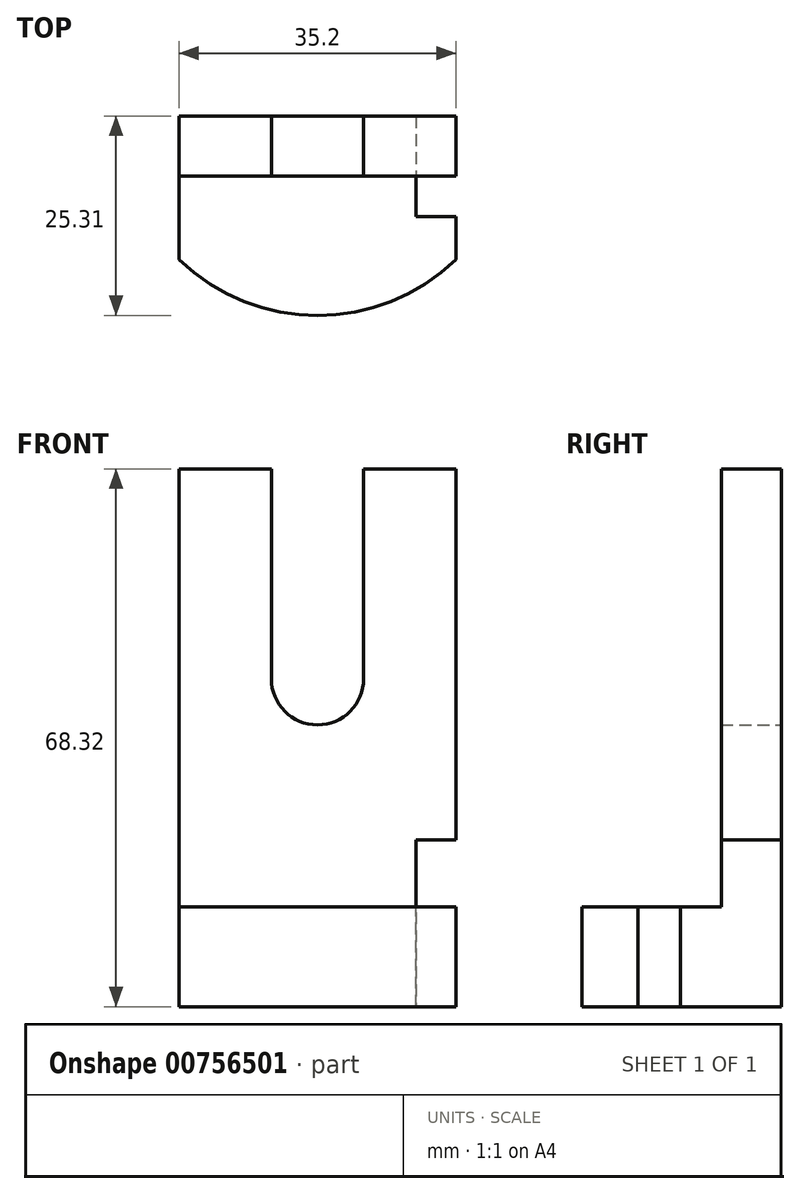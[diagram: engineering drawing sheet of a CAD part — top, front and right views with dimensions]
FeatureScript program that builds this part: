
annotation { "Feature Type Name" : "Feature", "Feature Type Description" : "" }
export const myFeature = defineFeature(function(context is Context, id is Id, definition is map)
    precondition{}
    {
        {
            var Q0;
            Q0=qCreatedBy(makeId("Top.planeOp"),FACE);
            var sketch = newSketch(context, id + "F0", { "sketchPlane" : qUnion([Q0])});
            skLineSegment(sketch, "E0", {"start": v(17.6, 0) * mm, "end": v(-17.6, 0) * mm});
            skLineSegment(sketch, "E1", {"start": v(-17.6, 0) * mm, "end": v(-17.6, -18.2) * mm});
            skArc(sketch, "E2", {"start": v(-17.6, -18.2) * mm, "mid": v(0, -25.31) * mm, "end": v(17.6, -18.2) * mm});
            skLineSegment(sketch, "E3", {"start": v(17.6, 0) * mm, "end": v(17.6, -18.2) * mm});
            skSolve(sketch);
        }
        {
            var Q0;
            Q0 = qSketchRegion(id + "F0", true);
            extrude(context, id + "F1", {"entities" : qUnion([Q0]), "depth" : 12.7 * mm, "offsetDistance" : 25.4 * mm});
        }
        {
            var Q0;
            Q0=qCreatedBy(makeId("Front.planeOp"),FACE);
            var sketch = newSketch(context, id + "F2", { "sketchPlane" : qUnion([Q0])});
            skLineSegment(sketch, "E4", {"start": v(17.6, 12.7) * mm, "end": v(17.6, 68.32) * mm});
            skLineSegment(sketch, "E5", {"start": v(17.6, 68.32) * mm, "end": v(5.87, 68.32) * mm});
            skLineSegment(sketch, "E6", {"start": v(-17.6, 68.32) * mm, "end": v(-17.6, 12.7) * mm});
            skLineSegment(sketch, "E7", {"start": v(-17.6, 12.7) * mm, "end": v(17.6, 12.7) * mm});
            skLineSegment(sketch, "E8", {"start": v(5.87, 68.32) * mm, "end": v(5.87, 41.66) * mm});
            skArc(sketch, "E9", {"start": v(5.87, 41.66) * mm, "mid": v(0, 35.8) * mm, "end": v(-5.87, 41.66) * mm});
            skLineSegment(sketch, "E10", {"start": v(-5.87, 41.66) * mm, "end": v(-5.87, 68.32) * mm});
            skLineSegment(sketch, "E11.trimOffspring", {"start": v(-5.87, 68.32) * mm, "end": v(-17.6, 68.32) * mm});
            skSolve(sketch);
        }
        {
            var Q0;
            Q0 = qSketchRegion(id + "F2", true);
            extrude(context, id + "F3", {"entities" : qUnion([Q0]), "operationType" : NewBodyOperationType.ADD, "depth" : 7.62 * mm, "offsetDistance" : 25.4 * mm});
        }
        {
            var Q0;
            Q0=makeQuery(id+"F3.boolean.opBoolean","MERGE",FACE,{"derivedFrom":[makeQuery(id+"F1.opExtrude","SWEPT_FACE",FACE,{"disambiguationData":[OSD([sQuery(id+"F0.wireOp",EDGE,"E3")])]}),makeQuery(id+"F3.opExtrude","SWEPT_FACE",FACE,{"disambiguationData":[OSD([sQuery(id+"F2.wireOp",EDGE,"E4")])]})]});
            var sketch = newSketch(context, id + "F4", { "sketchPlane" : qUnion([Q0])});
            skLineSegment(sketch, "E12.bottom", {"start": v(0, 0) * mm, "end": v(-12.78, 0) * mm});
            skLineSegment(sketch, "E12.top", {"start": v(0, 21.2) * mm, "end": v(-12.78, 21.2) * mm});
            skLineSegment(sketch, "E12.left", {"start": v(0, 0) * mm, "end": v(0, 21.2) * mm});
            skLineSegment(sketch, "E12.right", {"start": v(-12.78, 0) * mm, "end": v(-12.78, 21.2) * mm});
            skSolve(sketch);
        }
        {
            var Q0;
            Q0 = qSketchRegion(id + "F4", true);
            extrude(context, id + "F5", {"entities" : qUnion([Q0]), "operationType" : NewBodyOperationType.REMOVE, "oppositeDirection" : true, "depth" : 5.08 * mm, "offsetDistance" : 25.4 * mm});
        }
    });
